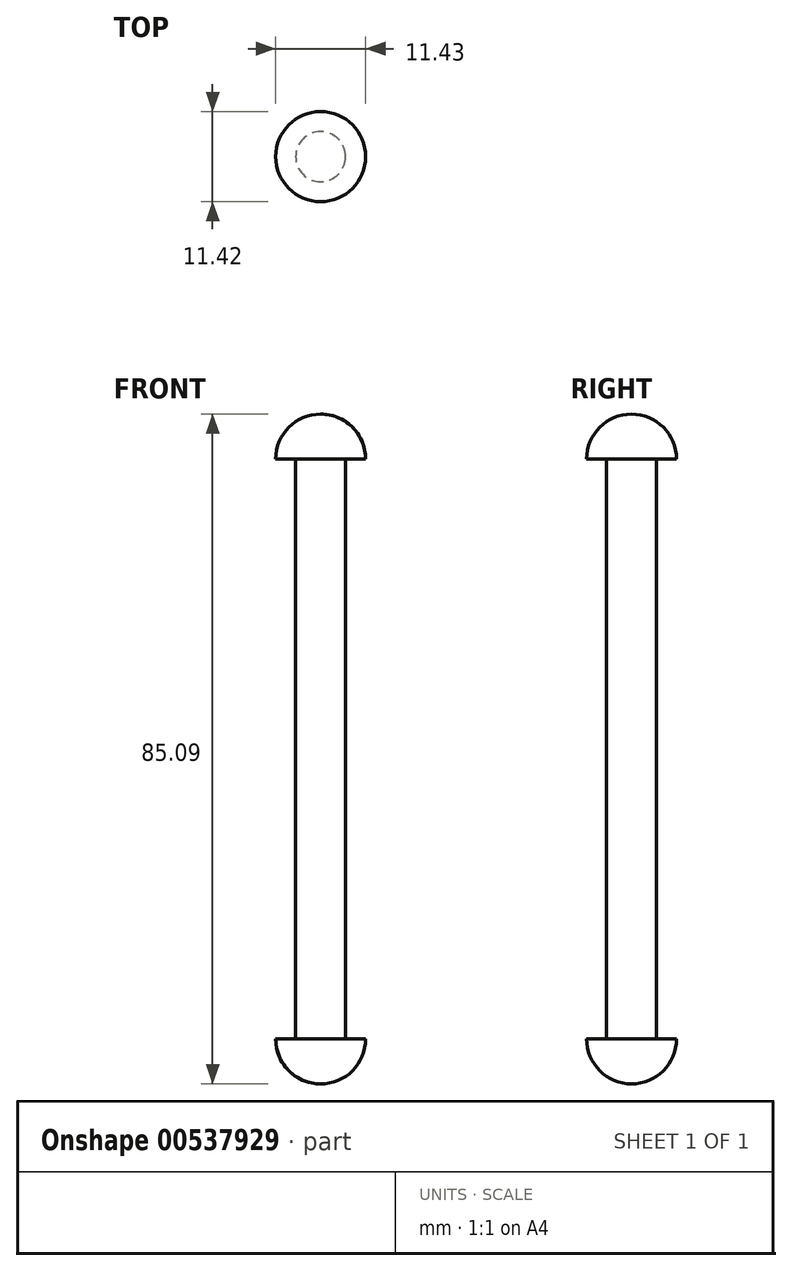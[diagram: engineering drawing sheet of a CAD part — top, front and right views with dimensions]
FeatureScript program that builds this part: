
annotation { "Feature Type Name" : "Feature", "Feature Type Description" : "" }
export const myFeature = defineFeature(function(context is Context, id is Id, definition is map)
    precondition{}
    {
        {
            var Q0;
            Q0=qCreatedBy(makeId("Front.planeOp"),FACE);
            var sketch = newSketch(context, id + "F0", { "sketchPlane" : qUnion([Q0])});
            skLineSegment(sketch, "E0", {"start": v(0, 0) * mm, "end": v(0, 85.1) * mm});
            skPoint(sketch, "E1.visualSharp", {"position": v(5.77, 0) * mm});
            skLineSegment(sketch, "E2.0", {"start": v(3.18, 5.72) * mm, "end": v(3.18, 79.38) * mm});
            skLineSegment(sketch, "E3", {"start": v(0, 85.1) * mm, "end": v(0, 85.1) * mm});
            skLineSegment(sketch, "E4", {"start": v(0, 0) * mm, "end": v(0, 0) * mm});
            skLineSegment(sketch, "E5.0", {"start": v(3.18, 5.72) * mm, "end": v(5.72, 5.72) * mm});
            skPoint(sketch, "E6.visualSharp", {"position": v(5.71, 85.1) * mm});
            skArc(sketch, "E6.filletArc", {"start": v(5.72, 79.38) * mm, "mid": v(4.04, 83.42) * mm, "end": v(0, 85.1) * mm});
            skArc(sketch, "E7.filletArc", {"start": v(0, 0) * mm, "mid": v(4.04, 1.67) * mm, "end": v(5.72, 5.71) * mm});
            skLineSegment(sketch, "E8", {"start": v(3.18, 79.38) * mm, "end": v(5.72, 79.38) * mm});
            skSolve(sketch);
        }
        {
            var Q0;
            Q0=makeQuery(id+"F0.imprint","IMPRINT",FACE,{"disambiguationData":[TD([[makeQuery(id+"F0.imprint","IMPRINT",EDGE,{"derivedFrom":sQuery(id+"F0.wireOp",EDGE,"E0")}),-1.0]])]});
            var Q1;
            Q1=sQuery(id+"F0.wireOp",EDGE,"E0");
            var Q2;
            Q2=sQuery(id+"F0.wireOp",EDGE,"E6.filletArc");
            var Q3;
            Q3=sQuery(id+"F0.wireOp",EDGE,"E8");
            var Q4;
            Q4=sQuery(id+"F0.wireOp",EDGE,"E2.0");
            var Q5;
            Q5=sQuery(id+"F0.wireOp",EDGE,"E5.0");
            var Q6;
            Q6=sQuery(id+"F0.wireOp",EDGE,"E7.filletArc");
            var Q7;
            Q7=sQuery(id+"F0.wireOp",EDGE,"E0");
            revolve(context, id + "F1", {"entities" : qUnion([Q0]), "surfaceEntities" : qUnion([Q1, Q2, Q3, Q4, Q5, Q6]), "axis" : qUnion([Q7]), "revolveType" : RevolveType.FULL});
        }
    });
